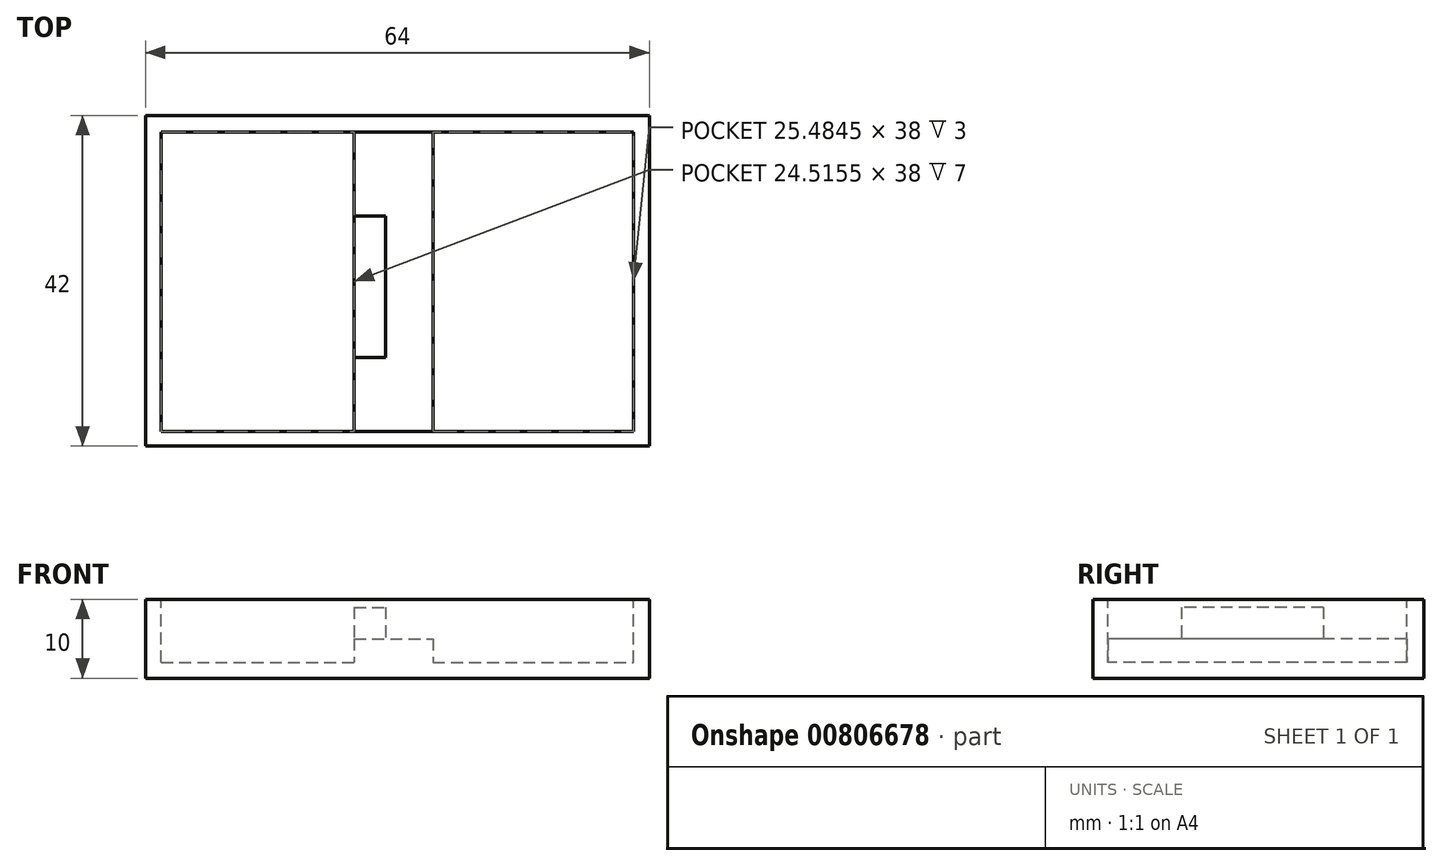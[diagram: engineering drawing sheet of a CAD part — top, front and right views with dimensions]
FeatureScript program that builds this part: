
annotation { "Feature Type Name" : "Feature", "Feature Type Description" : "" }
export const myFeature = defineFeature(function(context is Context, id is Id, definition is map)
    precondition{}
    {
        {
            var Q0;
            Q0=qCreatedBy(makeId("Top.planeOp"),FACE);
            var sketch = newSketch(context, id + "F0", { "sketchPlane" : qUnion([Q0])});
            skLineSegment(sketch, "E0.bottom", {"start": v(-68.17, 46.71) * mm, "end": v(-4.17, 46.71) * mm});
            skLineSegment(sketch, "E0.top", {"start": v(-68.17, 4.71) * mm, "end": v(-4.17, 4.71) * mm});
            skLineSegment(sketch, "E0.left", {"start": v(-68.17, 46.71) * mm, "end": v(-68.17, 4.71) * mm});
            skLineSegment(sketch, "E0.right", {"start": v(-4.17, 46.71) * mm, "end": v(-4.17, 4.71) * mm});
            skSolve(sketch);
        }
        {
            var Q0;
            Q0=makeQuery(id+"F0.imprint","IMPRINT",FACE,{"disambiguationData":[TD([[makeQuery(id+"F0.imprint","IMPRINT",EDGE,{"derivedFrom":sQuery(id+"F0.wireOp",EDGE,"E0.bottom")}),-1.0]])]});
            extrude(context, id + "F1", {"entities" : qUnion([Q0]), "depth" : 10 * mm, "offsetDistance" : 25 * mm});
        }
        {
            var Q0;
            Q0=makeQuery(id+"F1.opExtrude","CAP_FACE",FACE,{"disambiguationData":[OSD([sQuery(id+"F0.wireOp",EDGE,"E0.bottom"),sQuery(id+"F0.wireOp",EDGE,"E0.top"),sQuery(id+"F0.wireOp",EDGE,"E0.left"),sQuery(id+"F0.wireOp",EDGE,"E0.right")])],"isStart":false});
            var sketch = newSketch(context, id + "F2", { "sketchPlane" : qUnion([Q0])});
            skLineSegment(sketch, "E1.bottom", {"start": v(-66.17, 44.58) * mm, "end": v(-6.17, 44.58) * mm});
            skLineSegment(sketch, "E1.top", {"start": v(-66.17, 6.58) * mm, "end": v(-6.17, 6.58) * mm});
            skLineSegment(sketch, "E1.left", {"start": v(-66.17, 44.58) * mm, "end": v(-66.17, 6.58) * mm});
            skLineSegment(sketch, "E1.right", {"start": v(-6.17, 44.58) * mm, "end": v(-6.17, 6.58) * mm});
            skSolve(sketch);
        }
        {
            var Q0;
            Q0 = qSketchRegion(id + "F2", true);
            extrude(context, id + "F3", {"entities" : qUnion([Q0]), "operationType" : NewBodyOperationType.REMOVE, "oppositeDirection" : true, "depth" : 8 * mm, "offsetDistance" : 25 * mm});
        }
        {
            var Q0;
            Q0=makeQuery(id+"F3.boolean.opBoolean","COPY",FACE,{"derivedFrom":makeQuery(id+"F3.opExtrude","CAP_FACE",FACE,{"disambiguationData":[OSD([sQuery(id+"F2.wireOp",EDGE,"E1.bottom"),sQuery(id+"F2.wireOp",EDGE,"E1.top"),sQuery(id+"F2.wireOp",EDGE,"E1.left"),sQuery(id+"F2.wireOp",EDGE,"E1.right")])],"isStart":false})});
            var sketch = newSketch(context, id + "F4", { "sketchPlane" : qUnion([Q0])});
            skLineSegment(sketch, "E2", {"start": v(-41.66, 44.58) * mm, "end": v(-41.66, 6.58) * mm});
            skLineSegment(sketch, "E3", {"start": v(-31.66, 44.58) * mm, "end": v(-31.66, 6.58) * mm});
            skSolve(sketch);
        }
        {
            var Q0;
            {var subQ0=sQuery(id+"F4.wireOp",EDGE,"E2");Q0=makeQuery(id+"F4.imprint","IMPRINT",FACE,{"disambiguationData":[TD([[makeQuery(id+"F4.imprint","IMPRINT",EDGE,{"derivedFrom":subQ0}),1.0]])]});}
            extrude(context, id + "F5", {"entities" : qUnion([Q0]), "operationType" : NewBodyOperationType.ADD, "depth" : 3 * mm, "offsetDistance" : 25 * mm});
        }
        {
            var Q0;
            Q0=makeQuery(id+"F5.opExtrude","CAP_FACE",FACE,{"disambiguationData":[OSD([sQuery(id+"F2.wireOp",EDGE,"E1.bottom"),sQuery(id+"F2.wireOp",EDGE,"E1.top"),sQuery(id+"F4.wireOp",EDGE,"E2"),sQuery(id+"F4.wireOp",EDGE,"E3")])],"isStart":false});
            var sketch = newSketch(context, id + "F6", { "sketchPlane" : qUnion([Q0])});
            skLineSegment(sketch, "E4.bottom", {"start": v(-41.66, 33.94) * mm, "end": v(-37.66, 33.94) * mm});
            skLineSegment(sketch, "E4.top", {"start": v(-41.66, 15.94) * mm, "end": v(-37.66, 15.94) * mm});
            skLineSegment(sketch, "E4.left", {"start": v(-41.66, 33.94) * mm, "end": v(-41.66, 15.94) * mm});
            skLineSegment(sketch, "E4.right", {"start": v(-37.66, 33.94) * mm, "end": v(-37.66, 15.94) * mm});
            skSolve(sketch);
        }
        {
            var Q0;
            Q0 = qSketchRegion(id + "F6", true);
            extrude(context, id + "F7", {"entities" : qUnion([Q0]), "operationType" : NewBodyOperationType.ADD, "depth" : 4 * mm, "offsetDistance" : 25 * mm});
        }
    });
